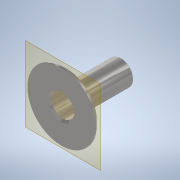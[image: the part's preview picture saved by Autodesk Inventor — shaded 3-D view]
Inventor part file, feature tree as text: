
AUTODESK INVENTOR PART (.ipt)
format: ipt  version: 2021 (Build 250183000, 183)  size: 161,280 bytes
history: native  units: mm
features: other x5, extrude x4, sketch x4, chamfer x3, reference x3
ambient origin geometry x8: Origin, YZ Plane, XZ Plane, XY Plane, X Axis, Y Axis, Z Axis, Center Point
bodies: Body1 (feature_tree)
feature tree (19):
  other  "Bryła1"
  other  "Oś konstrukcyjna1"
  other  "Płaszczyzna konstrukcyjna1"
  extrude  "Wyciągnięcie proste1"  Depth=145.0mm
  extrude  "Wyciągnięcie proste2"  Depth=60.0mm
  extrude  "Wyciągnięcie proste3"  Depth=5.0mm TaperAngle=0.0deg
  chamfer  "Faza1"  Distance=65.0mm
  chamfer  "Faza2"  Distance=150.0mm
  extrude  "Wyciągnięcie proste4"  Depth=3.0mm TaperAngle=0.0deg
  chamfer  "Faza3"  Distance=1.0mm Angle=45.0deg
  sketch  "Szkic1"
  reference  "Odniesienie1"
  reference  "Odniesienie2"
  sketch  "Szkic2"
  sketch  "Szkic3"
  sketch  "Szkic4"
  reference  "Odniesienie3"
  other  "Zespół1"
  other  "garnek:1"
